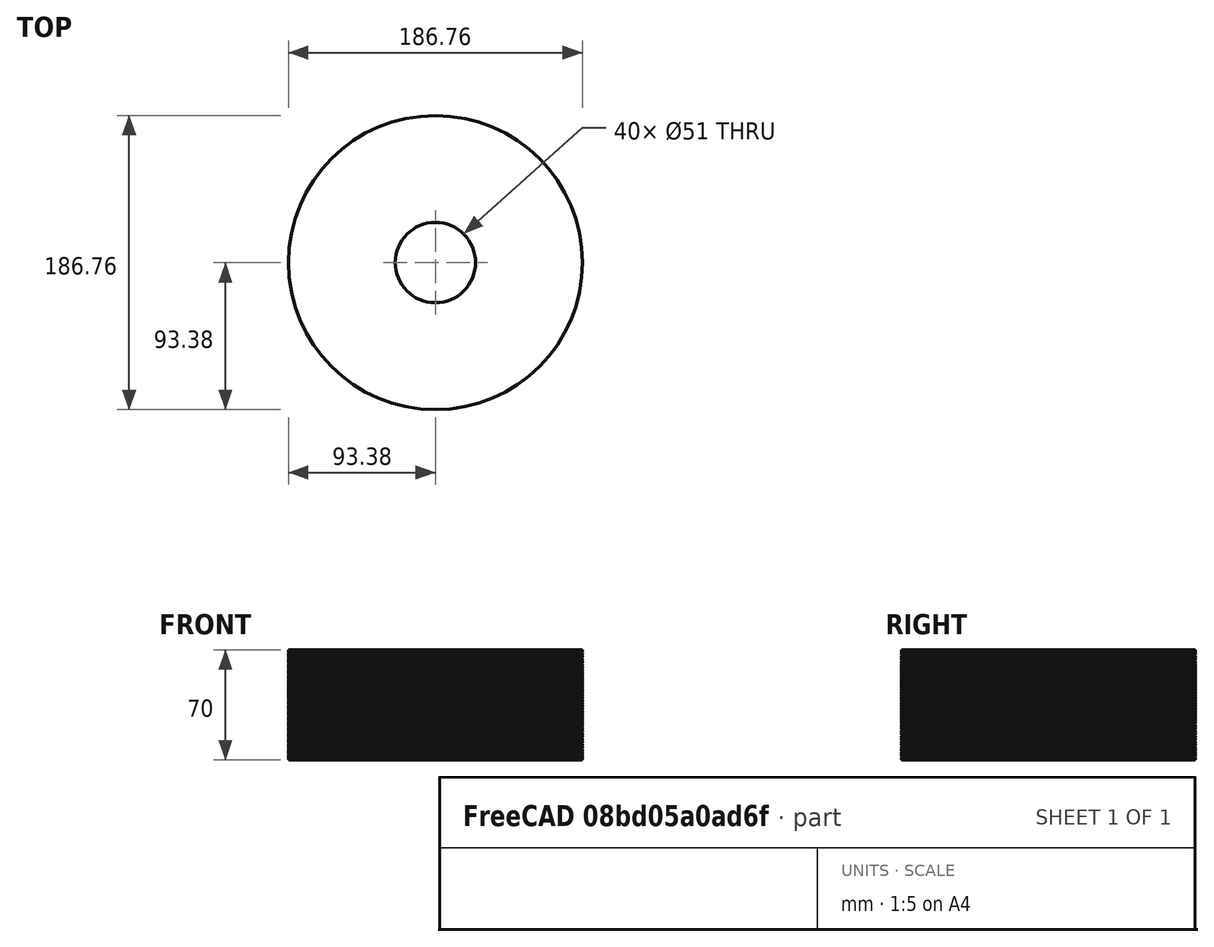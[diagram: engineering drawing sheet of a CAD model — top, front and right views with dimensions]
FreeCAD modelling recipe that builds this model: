
FCSTD DOCUMENT  (FreeCAD 0.14R3310 (Git))
Label: 43. FILAMENTO (1.75mm)
License: CC-BY 3.0
LicenseURL: http://creativecommons.org/licenses/by/3.0/
objects: Sketcher::SketchObject×1, PartDesign::Pad×1, PartDesign::Fillet×1, Part::FeaturePython×1
note: 5 computed .brp shape members not serialized (recipe doc carries the construction recipe); baked Part::Feature solids carry a one-line shape summary decoded from their .brp

FEATURE [Sketcher::SketchObject] Sketch
  sketch-geometry (2):
    g0: Circle CenterX=0 CenterY=0 CenterZ=0 NormalX=0 NormalY=0 NormalZ=1 Radius=25.5
    g1: Circle CenterX=0 CenterY=0 CenterZ=0 NormalX=0 NormalY=0 NormalZ=1 Radius=93.38
  constraints (4):
    c: Coincident(g0,g-1)
    c: Radius(g0) = 25.5
    c: Coincident(g1,g-1)
    c: Radius(g1) = 93.38
FEATURE [PartDesign::Pad] Pad
  Length = 1.75
  Length2 = 100
  Sketch = -> Sketch
  Type = 0
FEATURE [PartDesign::Fillet] Fillet
  Base = -> Pad [Edge2,Edge3]
  Radius = 0.85
FEATURE [Part::FeaturePython] Array  # Draft array (typed FeaturePython)
  Angle = 360
  ArrayType = 0
  Axis = (0,0,1)
  Base = -> Fillet
  Center = (0,0,0)
  IntervalX = (1,0,0)
  IntervalY = (0,1,0)
  IntervalZ = (0,0,1.75)
  NumberPolar = 1
  NumberX = 1
  NumberY = 1
  NumberZ = 40
